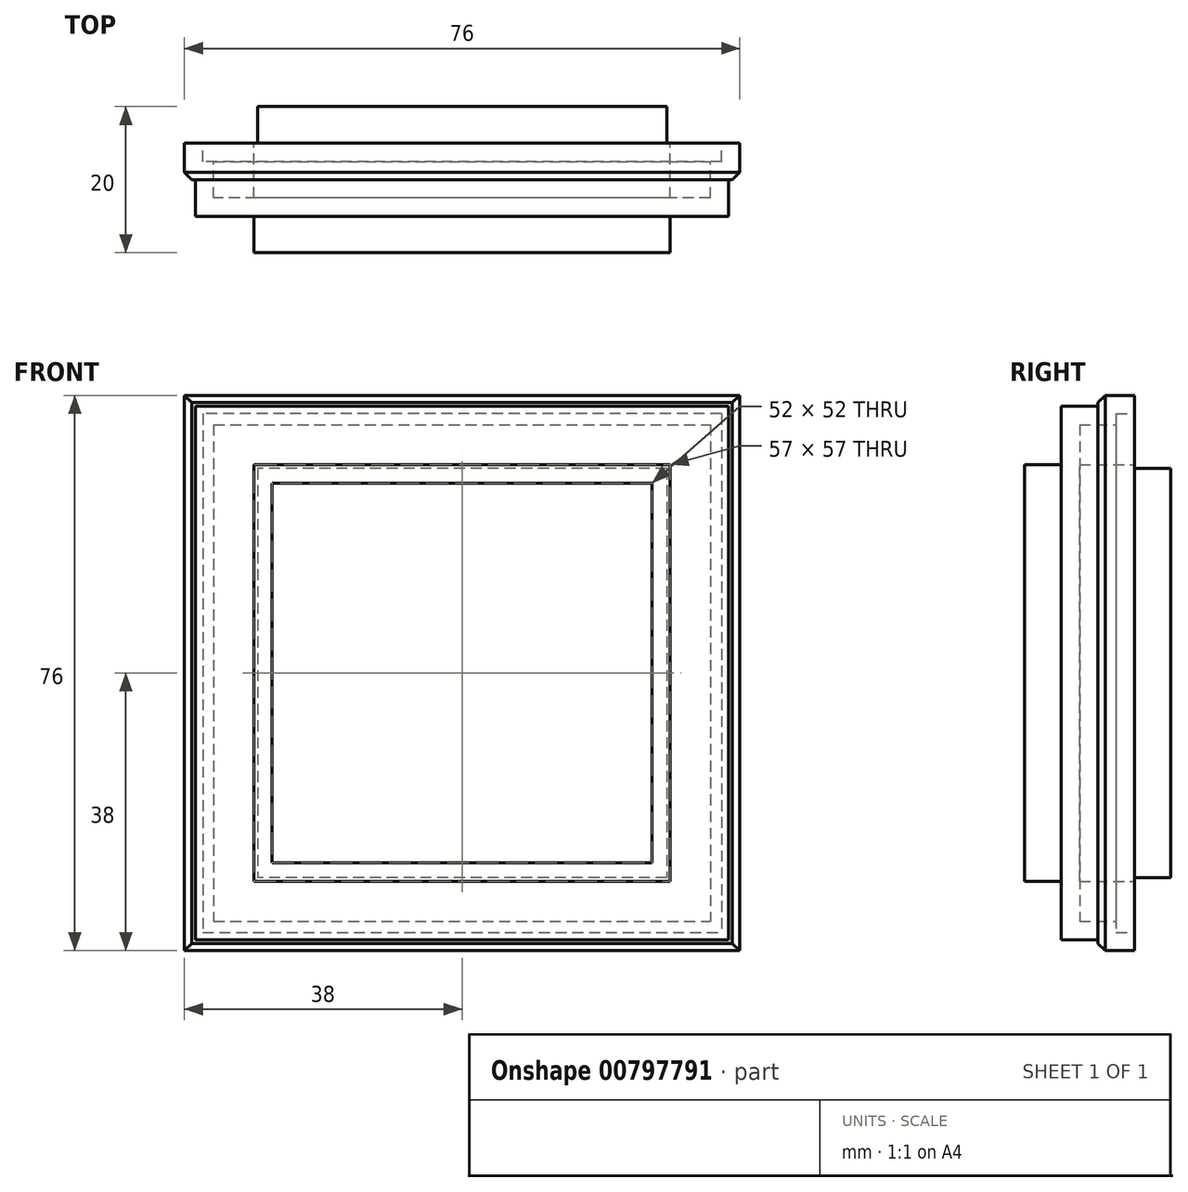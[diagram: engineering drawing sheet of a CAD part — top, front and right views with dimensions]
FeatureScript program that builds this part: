
annotation { "Feature Type Name" : "Feature", "Feature Type Description" : "" }
export const myFeature = defineFeature(function(context is Context, id is Id, definition is map)
    precondition{}
    {
        {
            var Q0;
            Q0=qCreatedBy(makeId("Front.planeOp"),FACE);
            var sketch = newSketch(context, id + "F0", { "sketchPlane" : qUnion([Q0])});
            skLineSegment(sketch, "E0.bottom", {"start": v(0, 0) * mm, "end": v(76, 0) * mm});
            skLineSegment(sketch, "E0.top", {"start": v(0, 76) * mm, "end": v(76, 76) * mm});
            skLineSegment(sketch, "E0.left", {"start": v(0, 0) * mm, "end": v(0, 76) * mm});
            skLineSegment(sketch, "E0.right", {"start": v(76, 0) * mm, "end": v(76, 76) * mm});
            skLineSegment(sketch, "E1.bottom", {"start": v(12, 64) * mm, "end": v(64, 64) * mm});
            skLineSegment(sketch, "E1.top", {"start": v(12, 12) * mm, "end": v(64, 12) * mm});
            skLineSegment(sketch, "E1.left", {"start": v(12, 64) * mm, "end": v(12, 12) * mm});
            skLineSegment(sketch, "E1.right", {"start": v(64, 64) * mm, "end": v(64, 12) * mm});
            skLineSegment(sketch, "E2.bottom", {"start": v(10, 66) * mm, "end": v(66, 66) * mm});
            skLineSegment(sketch, "E2.top", {"start": v(10, 10) * mm, "end": v(66, 10) * mm});
            skLineSegment(sketch, "E2.left", {"start": v(10, 66) * mm, "end": v(10, 10) * mm});
            skLineSegment(sketch, "E2.right", {"start": v(66, 66) * mm, "end": v(66, 10) * mm});
            skLineSegment(sketch, "E3.bottom", {"start": v(1.5, 74.5) * mm, "end": v(74.5, 74.5) * mm});
            skLineSegment(sketch, "E3.top", {"start": v(1.5, 1.5) * mm, "end": v(74.5, 1.5) * mm});
            skLineSegment(sketch, "E3.left", {"start": v(1.5, 74.5) * mm, "end": v(1.5, 1.5) * mm});
            skLineSegment(sketch, "E3.right", {"start": v(74.5, 74.5) * mm, "end": v(74.5, 1.5) * mm});
            skSolve(sketch);
        }
        {
            var Q0;
            Q0=makeQuery(id+"F0.imprint","IMPRINT",FACE,{"disambiguationData":[TD([[makeQuery(id+"F0.imprint","IMPRINT",EDGE,{"derivedFrom":sQuery(id+"F0.wireOp",EDGE,"E2.bottom")}),1.0]])]});
            var Q1;
            Q1=makeQuery(id+"F0.imprint","IMPRINT",FACE,{"disambiguationData":[TD([[makeQuery(id+"F0.imprint","IMPRINT",EDGE,{"derivedFrom":sQuery(id+"F0.wireOp",EDGE,"E1.bottom")}),1.0]])]});
            extrude(context, id + "F1", {"entities" : qUnion([Q0, Q1]), "depth" : 20 * mm, "offsetDistance" : 25 * mm});
        }
        {
            var Q0;
            Q0 = qSketchRegion(id + "F0", true);
            extrude(context, id + "F2", {"entities" : qUnion([Q0]), "operationType" : NewBodyOperationType.ADD, "depth" : 3 * mm, "offsetDistance" : 25 * mm});
        }
        {
            var Q0;
            Q0 = qSketchRegion(id + "F0", true);
            extrude(context, id + "F3", {"entities" : qUnion([Q0]), "operationType" : NewBodyOperationType.ADD, "depth" : 10 * mm, "offsetDistance" : 25 * mm});
        }
        {
            var Q0;
            Q0=qCreatedBy(makeId("Top.planeOp"),FACE);
            var sketch = newSketch(context, id + "F4", { "sketchPlane" : qUnion([Q0])});
            skPoint(sketch, "E4", {"position": v(0, -5) * mm});
            skLineSegment(sketch, "E5", {"start": v(0, -5) * mm, "end": v(76, -5) * mm});
            skLineSegment(sketch, "E6.bottom", {"start": v(0, -5) * mm, "end": v(10, -5) * mm});
            skLineSegment(sketch, "E6.top", {"start": v(0, 0) * mm, "end": v(10, 0) * mm});
            skLineSegment(sketch, "E6.left", {"start": v(0, -5) * mm, "end": v(0, 0) * mm});
            skLineSegment(sketch, "E6.right", {"start": v(10, -5) * mm, "end": v(10, 0) * mm});
            skLineSegment(sketch, "E7.bottom", {"start": v(76, -5) * mm, "end": v(66, -5) * mm});
            skLineSegment(sketch, "E7.top", {"start": v(76, 0) * mm, "end": v(66, 0) * mm});
            skLineSegment(sketch, "E7.left", {"start": v(76, -5) * mm, "end": v(76, 0) * mm});
            skLineSegment(sketch, "E7.right", {"start": v(66, -5) * mm, "end": v(66, 0) * mm});
            skSolve(sketch);
        }
        {
            var Q0;
            Q0=makeQuery(id+"F4.imprint","IMPRINT",FACE,{"disambiguationData":[TD([[makeQuery(id+"F4.imprint","IMPRINT",EDGE,{"derivedFrom":sQuery(id+"F4.wireOp",EDGE,"E6.top")}),-1.0]])]});
            var Q1;
            Q1=makeQuery(id+"F4.imprint","IMPRINT",FACE,{"disambiguationData":[TD([[makeQuery(id+"F4.imprint","IMPRINT",EDGE,{"derivedFrom":sQuery(id+"F4.wireOp",EDGE,"E7.top")}),1.0]])]});
            extrude(context, id + "F5", {"entities" : qUnion([Q0, Q1]), "operationType" : NewBodyOperationType.REMOVE, "depth" : 80 * mm, "offsetDistance" : 25 * mm});
        }
        {
            var Q0;
            Q0=qCreatedBy(makeId("Right.planeOp"),FACE);
            var sketch = newSketch(context, id + "F6", { "sketchPlane" : qUnion([Q0])});
            skPoint(sketch, "E8", {"position": v(-5, 0) * mm});
            skLineSegment(sketch, "E9.bottom", {"start": v(-5, 0) * mm, "end": v(0, 0) * mm});
            skLineSegment(sketch, "E9.top", {"start": v(-5, 10) * mm, "end": v(0, 10) * mm});
            skLineSegment(sketch, "E9.left", {"start": v(-5, 0) * mm, "end": v(-5, 10) * mm});
            skLineSegment(sketch, "E9.right", {"start": v(0, 0) * mm, "end": v(0, 10) * mm});
            skPoint(sketch, "E10", {"position": v(-5, 76) * mm});
            skLineSegment(sketch, "E11.bottom", {"start": v(-5, 76) * mm, "end": v(0, 76) * mm});
            skLineSegment(sketch, "E11.top", {"start": v(-5, 66) * mm, "end": v(0, 66) * mm});
            skLineSegment(sketch, "E11.left", {"start": v(-5, 76) * mm, "end": v(-5, 66) * mm});
            skLineSegment(sketch, "E11.right", {"start": v(0, 76) * mm, "end": v(0, 66) * mm});
            skSolve(sketch);
        }
        {
            var Q0;
            Q0=makeQuery(id+"F6.imprint","IMPRINT",FACE,{"disambiguationData":[TD([[makeQuery(id+"F6.imprint","IMPRINT",EDGE,{"derivedFrom":sQuery(id+"F6.wireOp",EDGE,"E9.bottom")}),1.0]])]});
            var Q1;
            Q1=makeQuery(id+"F6.imprint","IMPRINT",FACE,{"disambiguationData":[TD([[makeQuery(id+"F6.imprint","IMPRINT",EDGE,{"derivedFrom":sQuery(id+"F6.wireOp",EDGE,"E11.bottom")}),-1.0]])]});
            extrude(context, id + "F7", {"entities" : qUnion([Q0, Q1]), "operationType" : NewBodyOperationType.REMOVE, "depth" : 80 * mm, "offsetDistance" : 25 * mm});
        }
        {
            var Q0;
            Q0=qCreatedBy(makeId("Top.planeOp"),FACE);
            var sketch = newSketch(context, id + "F8", { "sketchPlane" : qUnion([Q0])});
            skPoint(sketch, "E12", {"position": v(1.5, -15) * mm});
            skLineSegment(sketch, "E13.bottom", {"start": v(1.5, -15) * mm, "end": v(9.5, -15) * mm});
            skLineSegment(sketch, "E13.top", {"start": v(1.5, -20) * mm, "end": v(9.5, -20) * mm});
            skLineSegment(sketch, "E13.left", {"start": v(1.5, -15) * mm, "end": v(1.5, -20) * mm});
            skLineSegment(sketch, "E13.right", {"start": v(9.5, -15) * mm, "end": v(9.5, -20) * mm});
            skPoint(sketch, "E14", {"position": v(74.5, -15) * mm});
            skLineSegment(sketch, "E15.bottom", {"start": v(74.5, -15) * mm, "end": v(66.5, -15) * mm});
            skLineSegment(sketch, "E15.top", {"start": v(74.5, -20) * mm, "end": v(66.5, -20) * mm});
            skLineSegment(sketch, "E15.left", {"start": v(74.5, -15) * mm, "end": v(74.5, -20) * mm});
            skLineSegment(sketch, "E15.right", {"start": v(66.5, -15) * mm, "end": v(66.5, -20) * mm});
            skSolve(sketch);
        }
        {
            var Q0;
            Q0=makeQuery(id+"F8.imprint","IMPRINT",FACE,{"disambiguationData":[TD([[makeQuery(id+"F8.imprint","IMPRINT",EDGE,{"derivedFrom":sQuery(id+"F8.wireOp",EDGE,"E13.bottom")}),-1.0]])]});
            var Q1;
            Q1=makeQuery(id+"F8.imprint","IMPRINT",FACE,{"disambiguationData":[TD([[makeQuery(id+"F8.imprint","IMPRINT",EDGE,{"derivedFrom":sQuery(id+"F8.wireOp",EDGE,"E15.bottom")}),1.0]])]});
            extrude(context, id + "F9", {"entities" : qUnion([Q0, Q1]), "operationType" : NewBodyOperationType.REMOVE, "depth" : 80 * mm, "offsetDistance" : 25 * mm});
        }
        {
            var Q0;
            Q0=qCreatedBy(makeId("Right.planeOp"),FACE);
            var sketch = newSketch(context, id + "F10", { "sketchPlane" : qUnion([Q0])});
            skPoint(sketch, "E16", {"position": v(-20, 1.5) * mm});
            skPoint(sketch, "E17", {"position": v(-20, 74.5) * mm});
            skLineSegment(sketch, "E18.bottom", {"start": v(-20, 1.5) * mm, "end": v(-15, 1.5) * mm});
            skLineSegment(sketch, "E18.top", {"start": v(-20, 9.5) * mm, "end": v(-15, 9.5) * mm});
            skLineSegment(sketch, "E18.left", {"start": v(-20, 1.5) * mm, "end": v(-20, 9.5) * mm});
            skLineSegment(sketch, "E18.right", {"start": v(-15, 1.5) * mm, "end": v(-15, 9.5) * mm});
            skLineSegment(sketch, "E19.bottom", {"start": v(-20, 74.5) * mm, "end": v(-15, 74.5) * mm});
            skLineSegment(sketch, "E19.top", {"start": v(-20, 66.5) * mm, "end": v(-15, 66.5) * mm});
            skLineSegment(sketch, "E19.left", {"start": v(-20, 74.5) * mm, "end": v(-20, 66.5) * mm});
            skLineSegment(sketch, "E19.right", {"start": v(-15, 74.5) * mm, "end": v(-15, 66.5) * mm});
            skSolve(sketch);
        }
        {
            var Q0;
            Q0 = qSketchRegion(id + "F10", true);
            extrude(context, id + "F11", {"entities" : qUnion([Q0]), "operationType" : NewBodyOperationType.REMOVE, "depth" : 80 * mm, "offsetDistance" : 25 * mm});
        }
        {
            var Q0;
            Q0=makeQuery(id+"F3.opExtrude","CAP_EDGE",EDGE,{"disambiguationData":[OSD([sQuery(id+"F0.wireOp",EDGE,"E0.bottom")])],"isStart":false});
            var Q1;
            Q1=makeQuery(id+"F3.opExtrude","CAP_EDGE",EDGE,{"disambiguationData":[OSD([sQuery(id+"F0.wireOp",EDGE,"E0.left")])],"isStart":false});
            var Q2;
            Q2=makeQuery(id+"F3.opExtrude","CAP_EDGE",EDGE,{"disambiguationData":[OSD([sQuery(id+"F0.wireOp",EDGE,"E0.right")])],"isStart":false});
            var Q3;
            Q3=makeQuery(id+"F3.opExtrude","CAP_EDGE",EDGE,{"disambiguationData":[OSD([sQuery(id+"F0.wireOp",EDGE,"E0.top")])],"isStart":false});
            var Q4;
            Q4=makeQuery(id+"F9.boolean.opBoolean","COPY",EDGE,{"derivedFrom":makeQuery(id+"F9.opExtrude","SWEPT_EDGE",EDGE,{"disambiguationData":[OSD([sQuery(id+"F8.wireOp",EDGE,"E15.top"),sQuery(id+"F8.wireOp",EDGE,"E15.right")])]})});
            var Q5;
            Q5=makeQuery(id+"F11.boolean.opBoolean","COPY",EDGE,{"derivedFrom":makeQuery(id+"F11.opExtrude","SWEPT_EDGE",EDGE,{"disambiguationData":[OSD([sQuery(id+"F10.wireOp",EDGE,"E19.top"),sQuery(id+"F10.wireOp",EDGE,"E19.left")])]})});
            var Q6;
            Q6=makeQuery(id+"F11.boolean.opBoolean","COPY",EDGE,{"derivedFrom":makeQuery(id+"F11.opExtrude","SWEPT_EDGE",EDGE,{"disambiguationData":[OSD([sQuery(id+"F10.wireOp",EDGE,"E18.top"),sQuery(id+"F10.wireOp",EDGE,"E18.left")])]})});
            var Q7;
            Q7=makeQuery(id+"F9.boolean.opBoolean","COPY",EDGE,{"derivedFrom":makeQuery(id+"F9.opExtrude","SWEPT_EDGE",EDGE,{"disambiguationData":[OSD([sQuery(id+"F8.wireOp",EDGE,"E13.top"),sQuery(id+"F8.wireOp",EDGE,"E13.right")])]})});
            chamfer(context, id + "F12", {"entities" : qUnion([Q0, Q1, Q2, Q3, Q4, Q5, Q6, Q7]), "width" : 1 * mm, "tangentPropagation" : true});
        }
        {
            var Q0;
            {var subQ0=sQuery(id+"F4.wireOp",EDGE,"E5");Q0=makeQuery(id+"F7.boolean.opBoolean","MERGE",FACE,{"derivedFrom":[makeQuery(id+"F5.boolean.opBoolean","COPY",FACE,{"derivedFrom":makeQuery(id+"F5.opExtrude","SWEPT_FACE",FACE,{"disambiguationData":[OSD([subQ0]),TDD([makeQuery(id+"F4.imprint","IMPRINT",EDGE,{"disambiguationData":[TD([[makeQuery(id+"F4.imprint","INTERSECT",VERTEX,{"derivedFrom":[subQ0,sQuery(id+"F4.wireOp",EDGE,"E7.left")]}),1.0]])],"derivedFrom":subQ0})])]})}),makeQuery(id+"F5.boolean.opBoolean","COPY",FACE,{"derivedFrom":makeQuery(id+"F5.opExtrude","SWEPT_FACE",FACE,{"disambiguationData":[OSD([subQ0]),TDD([makeQuery(id+"F4.imprint","IMPRINT",EDGE,{"disambiguationData":[TD([[makeQuery(id+"F4.imprint","INTERSECT",VERTEX,{"derivedFrom":[subQ0,sQuery(id+"F4.wireOp",EDGE,"E6.right")]}),1.0]])],"derivedFrom":subQ0})])]})})],"fromTools":[makeQuery(id+"F7.opExtrude","SWEPT_FACE",FACE,{"disambiguationData":[OSD([sQuery(id+"F6.wireOp",EDGE,"E9.left")])]}),makeQuery(id+"F7.opExtrude","SWEPT_FACE",FACE,{"disambiguationData":[OSD([sQuery(id+"F6.wireOp",EDGE,"E11.left")])]})]});}
            shell(context, id + "F13", {"entities" : qUnion([Q0]), "thickness" : 2.5 * mm});
        }
    });
